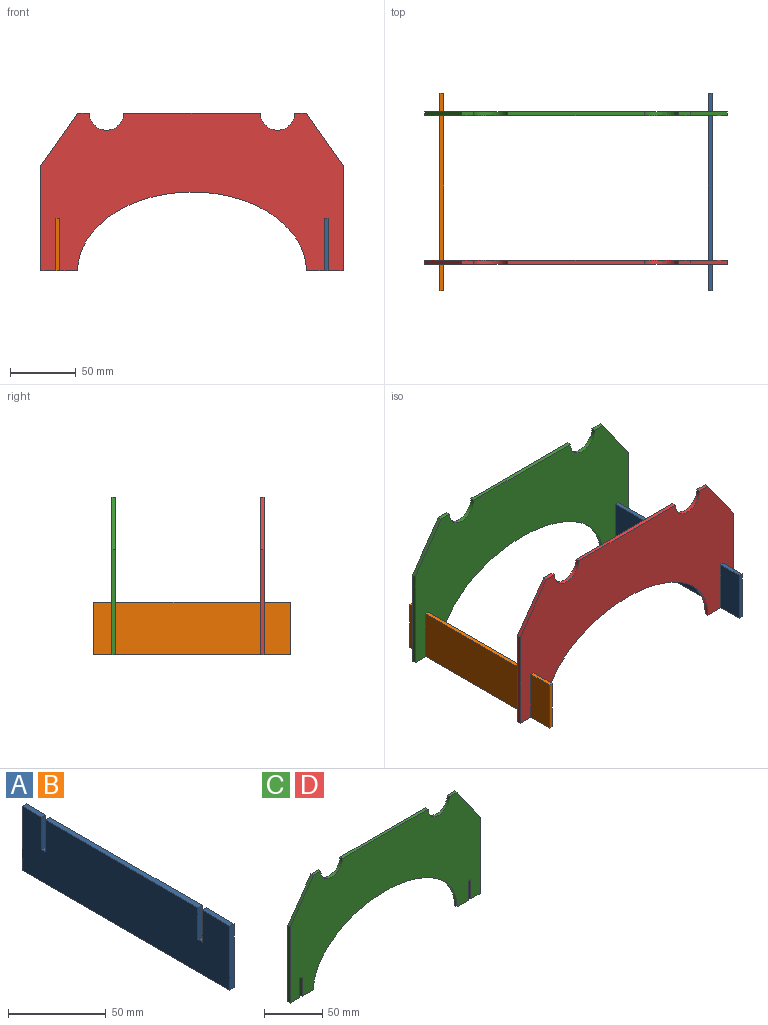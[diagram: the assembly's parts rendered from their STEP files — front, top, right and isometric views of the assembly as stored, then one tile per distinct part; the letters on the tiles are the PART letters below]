
ASSEMBLY  parts=4 mates=4
PART A: 14 faces, bbox 3x150x40 mm
  f0: plane 20x3mm, normal (0,1,0), area 60mm2, adj f1,f11,f12,f13
  f1: plane 110x3mm, normal (0,0,1), area 330mm2, adj f0,f2,f12,f13
  f2: plane 20x3mm, normal (0,-1,0), area 60mm2, adj f1,f3,f12,f13
  f3: plane 3x3mm, normal (0,0,1), area 9mm2, adj f2,f4,f12,f13
  f4: plane 20x3mm, normal (0,1,0), area 60mm2, adj f3,f5,f12,f13
  f5: plane 20x3mm, normal (0,0,1), area 60mm2, adj f4,f6,f12,f13
  f6: plane 40x3mm, normal (0,-1,0), area 120mm2, adj f5,f7,f12,f13
  f7: plane 150x3mm, normal (0,0,-1), area 450mm2, adj f6,f8,f12,f13
  f8: plane 40x3mm, normal (0,1,0), area 120mm2, adj f7,f9,f12,f13
  f9: plane 14x3mm, normal (0,0,1), area 42mm2, adj f8,f10,f12,f13
  f10: plane 20x3mm, normal (0,-1,0), area 60mm2, adj f9,f11,f12,f13
  f11: plane 3x3mm, normal (0,0,1), area 9mm2, adj f0,f10,f12,f13
  f12: plane 150x40mm, normal (1,0,0), area 5880mm2, adj f0,f1,f2,f3,f4,f5,f6,f7
  f13: plane 150x40mm, normal (-1,0,0), area 5880mm2, adj f0,f1,f2,f3,f4,f5,f6,f7
PART B: same geometry as A
PART C: 22 faces, bbox 230x3x120 mm
  f0: extruded ~174x60mm, area 698.6mm2, adj f1,f19,f20,f21
  f1: plane 13.62x3mm, normal (0,0,-1), area 40.8mm2, adj f0,f2,f20,f21
  f2: plane 20x3mm, normal (1,0,0), area 60mm2, adj f1,f3,f20,f21
  f3: plane 3x3mm, normal (0,0,-1), area 9mm2, adj f2,f4,f20,f21
  f4: plane 20x3mm, normal (-1,0,0), area 60mm2, adj f3,f5,f20,f21
  f5: plane 11.38x3mm, normal (0,0,-1), area 34.2mm2, adj f4,f6,f20,f21
  f6: plane 80x3mm, normal (1,0,0), area 240mm2, adj f5,f7,f20,f21
  f7: plane 40x28mm, normal (0.82,0,0.57), area 146.5mm2, adj f6,f8,f20,f21
  f8: plane 9x3mm, normal (0,0,1), area 27mm2, adj f7,f9,f20,f21
  f9: cylinder r=13mm len=26mm, axis (0,1,0), area 122.5mm2, adj f8,f10,f20,f21
  f10: plane 104x3mm, normal (0,0,1), area 312mm2, adj f9,f11,f20,f21
  f11: cylinder r=13mm len=26mm, axis (0,1,0), area 122.5mm2, adj f10,f12,f20,f21
  f12: plane 9x3mm, normal (0,0,1), area 27mm2, adj f11,f13,f20,f21
  f13: plane 40x28mm, normal (-0.82,0,0.57), area 146.5mm2, adj f12,f14,f20,f21
  f14: plane 80x3mm, normal (-1,0,0), area 240mm2, adj f13,f15,f20,f21
  f15: plane 11.38x3mm, normal (0,0,-1), area 34.2mm2, adj f14,f16,f20,f21
  f16: plane 20x3mm, normal (1,0,0), area 60mm2, adj f15,f17,f20,f21
  f17: plane 3x3mm, normal (0,0,-1), area 9mm2, adj f16,f18,f20,f21
  f18: plane 20x3mm, normal (-1,0,0), area 60mm2, adj f17,f19,f20,f21
  f19: plane 13.62x3mm, normal (0,0,-1), area 40.8mm2, adj f0,f18,f20,f21
  f20: plane 230x120mm, normal (0,-1,0), area 17629.5mm2, adj f0,f1,f2,f3,f4,f5,f6,f7
  f21: plane 230x120mm, normal (0,1,0), area 17629.5mm2, adj f0,f1,f2,f3,f4,f5,f6,f7
PART D: same geometry as C
PLACE A t=(200.73,-4.86,-4.26)mm
PLACE B t=(-3.5,-4.86,-4.26)mm
PLACE C t=(100.11,109.64,-4.26)mm
PLACE D t=(100.11,-3.36,-4.26)mm
MATE fastened A.f11 <-> C.f3  axis (0,0,1) through (202.23,108.14,-44.26)mm
MATE fastened D.f3 <-> A.f3  axis (0,0,-1) through (202.23,-4.86,-44.26)mm
MATE fastened C.f17 <-> B.f11  axis (0,0,-1) through (-2,108.14,-44.26)mm
MATE fastened B.f3 <-> D.f17  axis (0,0,1) through (-2,-4.86,-44.26)mm
